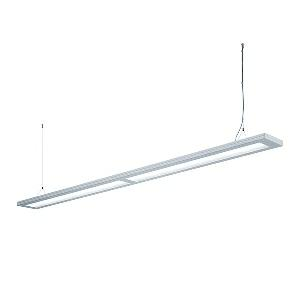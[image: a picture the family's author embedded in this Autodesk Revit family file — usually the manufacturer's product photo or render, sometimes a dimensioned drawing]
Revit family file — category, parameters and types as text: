
# Revit family: lavigo_-_dpp_13000_840_d_g2_00800704_96ae
name_source: partatom
category: Lighting Fixtures
units: mm (PartAtom-declared; Revit-internal decimal feet)

## family parameters
Cut with Voids When Loaded = No
Host = Face
Light Source = No
Part Type = Normal
Room Calculation Point = No
Round Connector Dimension = Use Diameter
Shared = No

## types (1)
- LAVIGO - DPP 13000/840/D/G2 (1 x LED, 13800 lm, 4000K)
    Apparent Load = 97 VA
    Approval mark = CE
    CIE Flux Codes = 60 87 97 25 100
    Color Rendering = 80-89
    Color Temperature = 4000K
    Control Gear = Electronic ballast
    Default Elevation = 1800 mm
    Description = DPP 13000/840/D/G2|Suspended luminaire|light source: LED|connected load: 220-240 V, 50/60 Hz|Power consumption: approx. 97 W|standby: approx. 0,50|luminous flux: 13800 lm|luminous efficacy: 142 lm/W|light distribution: Direct/indirect|direct ratio: approx. 25 %|colour temperature: Cold white, ca. 4000 K|color rendering index (CRI): >= 80|chromaticity tolerance:  3 SDCM|System of protection: IP 20|technology: Continuously dimmable|luminaire body|material: Steel/plastic|surface: Powder coatet|colour: Silver metallic|lamp cover: Polycarbonate (PC), Clear|mains lead: 1.00 m With free stranded wires|Fastening: Steel cable 0.3 - 0.7 m|decorative contrast side parts: Flint grey|glare control: Prism aperture|luminance(L65): <= 2700 cd/m|unified glare rating(4H 8H): <=  16|special features: Canopy colour (pure white), Cradle to Cradle Certified TM, DALI - dimming via digital rotary dimmer, DALI Load 2x, Direct light component with edge light and light-guide technology for homogenous light exit, Integration into DALI light management systems, Flicker-free, TouchDIM - dimming via standard switch|
    Frequency = 50 Hz
    Height = 36 mm
    Lamp = 1 x LED
    Lamp Light Flux = 13800 lm
    Lamp count = 1
    Length = 2430 mm
    Luminous efficacy = 142 lm/W
    Manufacturer = Waldmann
    ModVariant = No
    Model = 00800704
    Mounting Place = Ceiling
    Mounting Type = Pendant
    Number of Poles = 1
    OnlyDefault = Yes
    Power Factor = 1
    Product Name = LAVIGO - DPP 13000/840/D/G2
    Product group = Suspended luminaire
    ProductGroupID = 9
    Protection Class = Protection class I
    Protection Degree = IP 20
    RLX_Detail_Level = 1
    RLX_Emergency_Light_Flux = 0 lm
    RLX_Emergency_Type = 0
    RLX_Emergency_Type_DB = No
    RlxData = <blob elided: 26373 chars, md5=32c72f57>
    Socket = socket
    Standby Power = 0 W
    System Light Flux = 13800 lm
    System Power = 97 W
    Type Comments = Product without accessories
    Type Image = 121742000-00681441.jpg
    URL = http://relux.com
    VarID = ---
    Voltage = 230 V
    Voltage Range = 220-240 V
    Weight = 0.00 kg
    Width = 200 mm  [stored 0.656168 ft]

note: [stored X ft] marks values corroborated as IEEE doubles in the binary element streams (Revit-internal decimal feet)

## geometry (parser evidence)
native form markers: Blend x4, Sweep x13
no freeform markers — native parametric forms only
